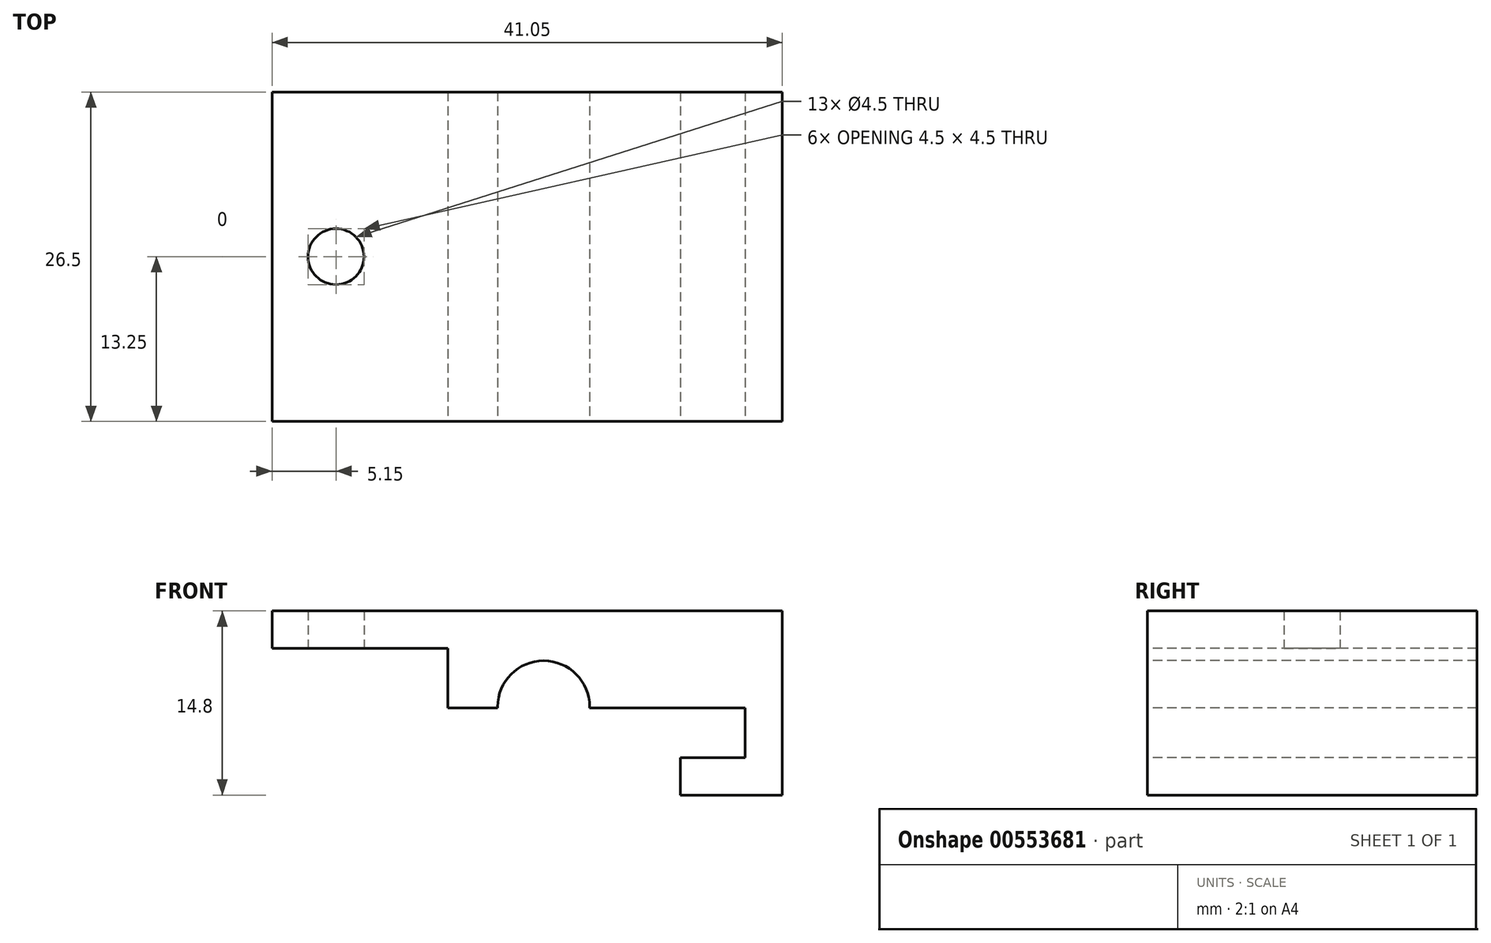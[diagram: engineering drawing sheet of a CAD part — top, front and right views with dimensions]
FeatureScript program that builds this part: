
annotation { "Feature Type Name" : "Feature", "Feature Type Description" : "" }
export const myFeature = defineFeature(function(context is Context, id is Id, definition is map)
    precondition{}
    {
        {
            var Q0;
            Q0=qCreatedBy(makeId("Front.planeOp"),FACE);
            var sketch = newSketch(context, id + "F0", { "sketchPlane" : qUnion([Q0])});
            skLineSegment(sketch, "E0", {"start": v(0, 15.4) * mm, "end": v(14.15, 15.4) * mm});
            skLineSegment(sketch, "E1", {"start": v(14.15, 15.4) * mm, "end": v(14.15, 10.6) * mm});
            skLineSegment(sketch, "E2", {"start": v(14.15, 10.6) * mm, "end": v(18.15, 10.6) * mm});
            skLineSegment(sketch, "E3", {"start": v(18.15, 10.6) * mm, "end": v(18.15, 10.7) * mm});
            skLineSegment(sketch, "E4", {"start": v(21.85, 14.4) * mm, "end": v(21.85, 14.4) * mm});
            skLineSegment(sketch, "E5", {"start": v(25.55, 10.7) * mm, "end": v(25.55, 10.6) * mm});
            skLineSegment(sketch, "E6", {"start": v(25.55, 10.6) * mm, "end": v(38.05, 10.6) * mm});
            skLineSegment(sketch, "E7", {"start": v(38.05, 10.6) * mm, "end": v(38.05, 6.6) * mm});
            skLineSegment(sketch, "E8", {"start": v(38.05, 6.6) * mm, "end": v(32.85, 6.6) * mm});
            skLineSegment(sketch, "E9", {"start": v(32.85, 6.6) * mm, "end": v(32.85, 3.6) * mm});
            skLineSegment(sketch, "E10", {"start": v(32.85, 3.6) * mm, "end": v(41.05, 3.6) * mm});
            skLineSegment(sketch, "E11", {"start": v(41.05, 3.6) * mm, "end": v(41.05, 18.4) * mm});
            skLineSegment(sketch, "E12", {"start": v(41.05, 18.4) * mm, "end": v(0, 18.4) * mm});
            skLineSegment(sketch, "E13", {"start": v(0, 18.4) * mm, "end": v(0, 15.4) * mm});
            skPoint(sketch, "E14.visualSharp", {"position": v(25.55, 14.4) * mm});
            skArc(sketch, "E14.filletArc", {"start": v(25.55, 10.7) * mm, "mid": v(24.47, 13.3) * mm, "end": v(21.85, 14.4) * mm});
            skPoint(sketch, "E15.visualSharp", {"position": v(18.15, 14.4) * mm});
            skArc(sketch, "E15.filletArc", {"start": v(21.85, 14.4) * mm, "mid": v(19.23, 13.3) * mm, "end": v(18.15, 10.7) * mm});
            skSolve(sketch);
        }
        {
            var Q0;
            Q0 = qSketchRegion(id + "F0", true);
            extrude(context, id + "F1", {"entities" : qUnion([Q0]), "oppositeDirection" : true, "depth" : 26.5 * mm, "offsetDistance" : 25 * mm});
        }
        {
            var Q0;
            Q0=makeQuery(id+"F1.opExtrude","SWEPT_FACE",FACE,{"disambiguationData":[OSD([sQuery(id+"F0.wireOp",EDGE,"E0")])]});
            var sketch = newSketch(context, id + "F2", { "sketchPlane" : qUnion([Q0])});
            skCircle(sketch, "E16", {"center": v(5.15, -13.25) * mm, "radius": 2.25 * mm});
            skSolve(sketch);
        }
        {
            var Q0;
            Q0=makeQuery(id+"F2.imprint","IMPRINT",FACE,{"disambiguationData":[TD([[makeQuery(id+"F2.imprint","IMPRINT",EDGE,{"derivedFrom":sQuery(id+"F2.wireOp",EDGE,"E16")}),1.0]])]});
            extrude(context, id + "F3", {"entities" : qUnion([Q0]), "operationType" : NewBodyOperationType.REMOVE, "endBound" : BoundingType.UP_TO_NEXT, "oppositeDirection" : true, "depth" : 25 * mm, "offsetDistance" : 25 * mm});
        }
    });
